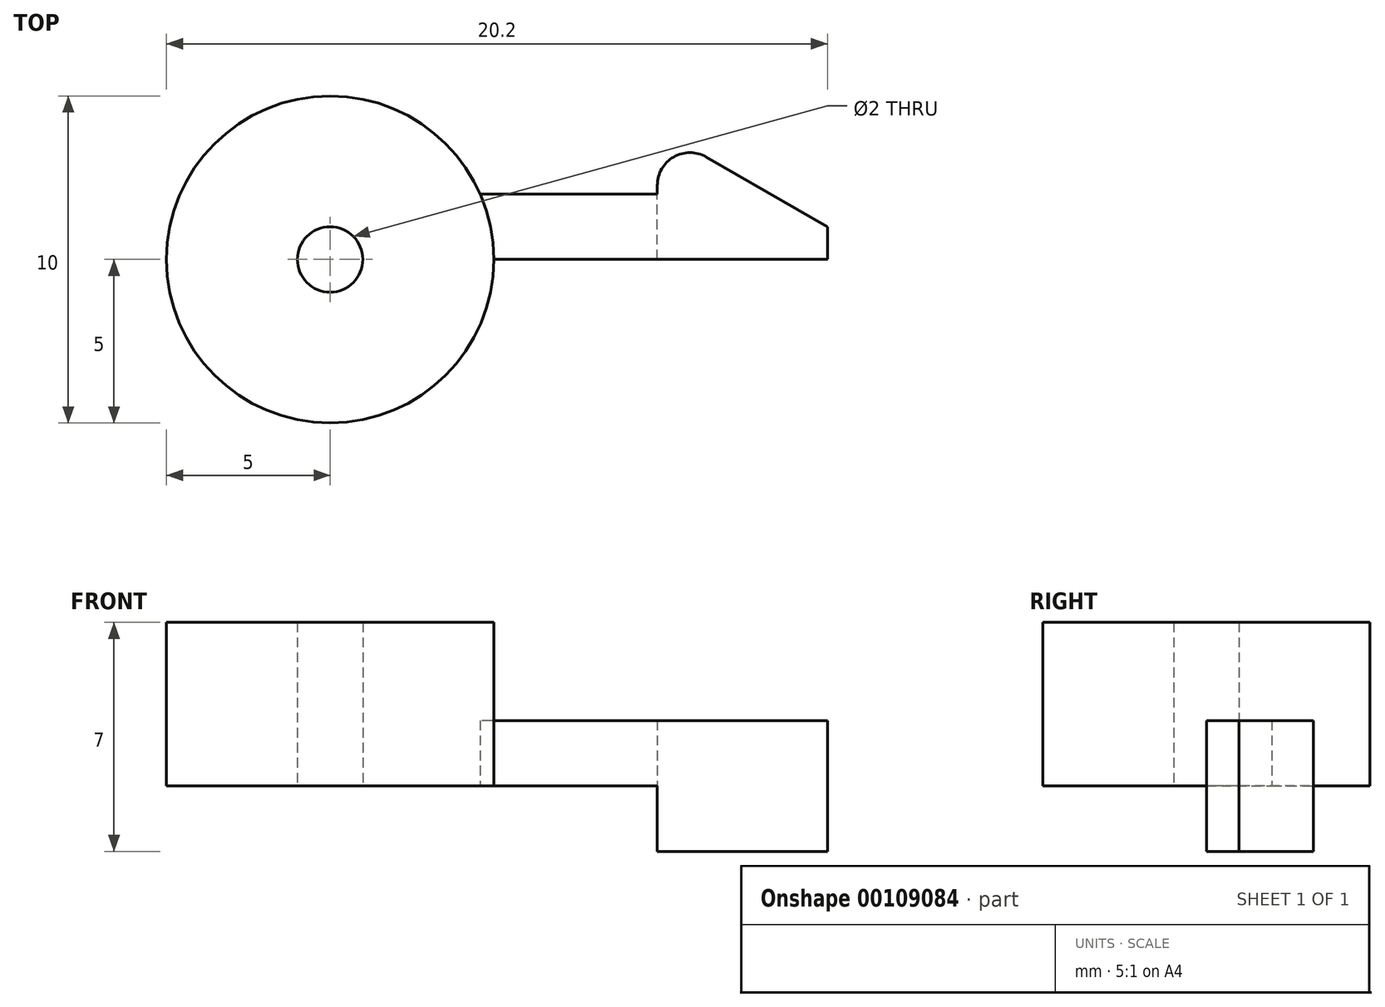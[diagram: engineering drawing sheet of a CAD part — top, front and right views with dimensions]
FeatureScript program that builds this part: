
annotation { "Feature Type Name" : "Feature", "Feature Type Description" : "" }
export const myFeature = defineFeature(function(context is Context, id is Id, definition is map)
    precondition{}
    {
        {
            var Q0;
            Q0=qCreatedBy(makeId("Top.planeOp"),FACE);
            var sketch = newSketch(context, id + "F0", { "sketchPlane" : qUnion([Q0])});
            skCircle(sketch, "E0", {"center": v(0, 0) * mm, "radius": 5 * mm});
            skLineSegment(sketch, "E1", {"start": v(10, 0) * mm, "end": v(10, 2) * mm});
            skLineSegment(sketch, "E2", {"start": v(10, 2) * mm, "end": v(4.58, 2) * mm});
            skLineSegment(sketch, "E3", {"start": v(10, 0) * mm, "end": v(5, 0) * mm});
            skLineSegment(sketch, "E4", {"start": v(10, 2) * mm, "end": v(10, 4) * mm});
            skLineSegment(sketch, "E5", {"start": v(10, 4) * mm, "end": v(15.2, 1) * mm});
            skLineSegment(sketch, "E6", {"start": v(15.2, 1) * mm, "end": v(15.2, 0) * mm});
            skLineSegment(sketch, "E7", {"start": v(15.2, 0) * mm, "end": v(10, 0) * mm});
            skSolve(sketch);
        }
        {
            var Q0;
            {var subQ0=sQuery(id+"F0.wireOp",EDGE,"E0");var subQ1=makeQuery(id+"F0.imprint","INTERSECT",VERTEX,{"derivedFrom":[subQ0,sQuery(id+"F0.wireOp",EDGE,"E2")]});Q0=makeQuery(id+"F0.imprint","IMPRINT",FACE,{"disambiguationData":[TD([[makeQuery(id+"F0.imprint","IMPRINT",EDGE,{"disambiguationData":[TD([[subQ1,1.0]])],"derivedFrom":subQ0}),1.0]])]});}
            extrude(context, id + "F1", {"entities" : qUnion([Q0]), "depth" : 5 * mm});
        }
        {
            var Q0;
            Q0=makeQuery(id+"F0.imprint","IMPRINT",FACE,{"disambiguationData":[TD([[makeQuery(id+"F0.imprint","IMPRINT",EDGE,{"derivedFrom":sQuery(id+"F0.wireOp",EDGE,"E1")}),1.0]])]});
            extrude(context, id + "F2", {"entities" : qUnion([Q0]), "operationType" : NewBodyOperationType.ADD, "depth" : 2 * mm});
        }
        {
            var Q0;
            Q0=makeQuery(id+"F0.imprint","IMPRINT",FACE,{"disambiguationData":[TD([[makeQuery(id+"F0.imprint","IMPRINT",EDGE,{"derivedFrom":sQuery(id+"F0.wireOp",EDGE,"E1")}),-1.0]])]});
            extrude(context, id + "F3", {"entities" : qUnion([Q0]), "operationType" : NewBodyOperationType.ADD, "endBound" : BoundingType.SYMMETRIC, "depth" : 4 * mm});
        }
        {
            var Q0;
            Q0=makeQuery(id+"F3.opExtrude","SWEPT_EDGE",EDGE,{"disambiguationData":[OSD([sQuery(id+"F0.wireOp",EDGE,"E4"),sQuery(id+"F0.wireOp",EDGE,"E5")])]});
            fillet(context, id + "F4", {"entities" : qUnion([Q0]), "radius" : 1 * mm, "tangentPropagation" : true, "allowEdgeOverflow" : false});
        }
        {
            var Q0;
            Q0=sQuery(id+"F0.wireOp",VERTEX,"E0.center");
            var Q1;
            Q1=makeQuery(id+"F1.opExtrude","SWEPT_BODY",BODY,{"disambiguationData":[OSD([sQuery(id+"F0.wireOp",EDGE,"E0")])]});
            hole(context, id + "F5", {"style" : HoleStyle.SIMPLE, "endStyle" : HoleEndStyle.THROUGH, "oppositeDirection" : true, "holeDiameter" : 2 * mm, "locations" : qUnion([Q0]), "scope" : qUnion([Q1]), "isTappedThrough" : true});
        }
    });
